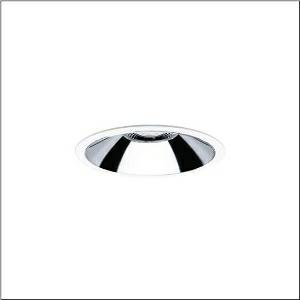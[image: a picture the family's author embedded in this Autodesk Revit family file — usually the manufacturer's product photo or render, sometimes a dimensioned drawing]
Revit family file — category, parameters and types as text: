
# Revit family: lunis_21_xl_51db15mf4d
name_source: partatom
category: Lighting Fixtures
units: mm (PartAtom-declared; Revit-internal decimal feet)

## family parameters
Cut with Voids When Loaded = No
Host = Face
Light Source = No
Part Type = Normal
Room Calculation Point = No
Round Connector Dimension = Use Diameter
Shared = No

## types (1)
- --- (1 x LED, 3000 lm, 24.3 W, 4000K)
    Apparent Load = 24 VA
    CIE Flux Codes = 89 99 100 100 100
    Color Rendering = 80
    Color Temperature = 4000K
    Default Elevation = 1800 mm
    Description = Lunis 21,  XL, downlight, of PC, light emission: direct distribution, LED rated luminous flux: 2.280lm, light colour: 840, control gear: ECG, with terminal, 3-pole, mains connection: 220..240V, AC, housing, round, of diecast aluminium, traffic white (RAL 9016), diameter: 213mm, protection rating (complete): IP20, insulation class (complete): insulation class II (safety insulation), certification: CE, impact resistance: IK02, packaging unit: 1 piece
    Height = 0 mm  [stored 0 ft]
    Lamp = 1 x LED
    Lamp Light Flux = 3000 lm
    Lamp Power = 24.3 W
    Lamp count = 1
    Length = 213 mm
    Luminous efficacy = 123 lm/W
    Manufacturer = Siteco
    ModVariant = No
    Model = 51DB15MF4D
    Mounting Place = Ceiling
    Mounting Type = Recessed
    Number of Poles = 1
    OnlyDefault = Yes
    Power Factor = 1
    Product Name = Lunis 21 XL
    Product group = downlight | ceiling recessed
    ProductGroupID = 402
    Protection Class = Protection class II
    Protection Degree = IP 20
    RLX_Detail_Level = 1
    RlxData = <blob elided: 27633 chars, md5=463db809>
    Socket = socket
    Standby Power = 0 W
    System Light Flux = 3000 lm
    System Power = 24 W
    Type Comments = factory setting: luminous flux: 100 % | (ON | ON)
    Type Image = l_1006990.jpg
    URL = http://relux.com
    VarID = @adj_060605
    Voltage = 0 V
    Weight = 0.00 kg
    Width = 0 mm  [stored 0 ft]

note: [stored X ft] marks values corroborated as IEEE doubles in the binary element streams (Revit-internal decimal feet)

## geometry (parser evidence)
native form markers: Blend x4, Sweep x10
no freeform markers — native parametric forms only
